# Revit family: Acoustic-Control_Wenger_Tunable-Panel
name_source: partatom
category: Generic Models
revit_build: Autodesk Revit 2016 (Build: 20161004_0715(x64)
units: mm (PartAtom-declared; Revit-internal decimal feet)

## family parameters
Always vertical = No
Can host rebar = No
Cut with Voids When Loaded = No
Part Type = Normal
Room Calculation Point = No
Round Connector Dimension = Use Diameter
Shared = No
Work Plane-Based = Yes

## types (6) — shared parameters
Assembly Code = E1020300
Construction Details = http://www.arcat.com
Default Elevation = 0' - 0"
Description = Wenger Wall Mounted Tunable Acoustic Panel - as Specified
Green Building-LEED = http://www.arcat.com
Keynote = 11 60 01
Manufacturer = Wenger Corporation
Manufacturer Website = https://www.wengercorp.com
Product Data = http://www.arcat.com
Revision = R1_2017-12
Sales Information = https://www.wengercorp.com
SpecWizard = http://www.arcat.com
Specification = http://www.arcat.com
Standards Conformance = Acoustical Performance ASTM C423-09a and E795-08  ;  Standard Fabric Class A Fire Rated ASTM E84
URL = https://www.wengercorp.com
Unit Depth = 1' - 0"
Unit Width = 4' - 0"
zero-valued in all types: Expected Lifespan (Years), Maintenance Schedule (Months), Warranty Duration (Years)

## per-type parameters (varying)
| type | Model | Tunable | Unit Height | Unit Weight | voidlocate |
| 4 x 8 Diffuser | Tunable Acoustic Panel Diffuser | No | 8' - 0" | 116 | 1' - 0" |
| 4 x 8 Absorber | Tunable Acoustic Panel Absorber | No | 8' - 0" | 110 | 1' - 0" |
| 4 x 8 Tunable Absorber Diffuser | Tunable Acoustic Panel Absorber Diffuser | Yes | 8' - 0" | 155 | 1' - 0" |
| 4 x 4 Diffuser | Tunable Acoustic Panel Diffuser | No | 4' - 0" | 72 | 2' - 0" |
| 4 x 4 Absorber | Tunable Acoustic Panel Absorber | No | 4' - 0" | 69 | 2' - 0" |
| 4 x 4 Tunable Absorber Diffuser | Tunable Acoustic Panel Absorber Diffuser | Yes | 4' - 0" | 92 | 2' - 0" |

## geometry (parser evidence)
native form markers: Sweep x3
no freeform markers — native parametric forms only
